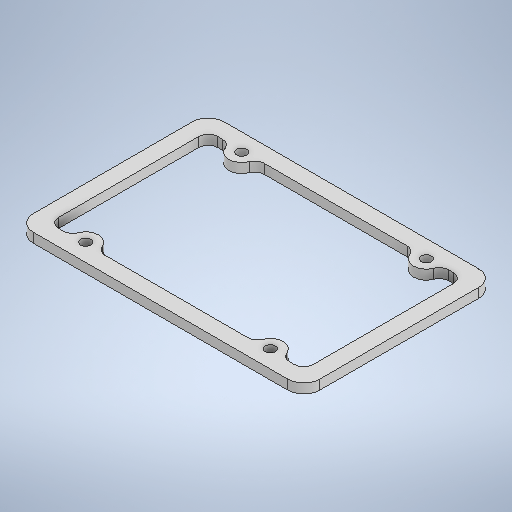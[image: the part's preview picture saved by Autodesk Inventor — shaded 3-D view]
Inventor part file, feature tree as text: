
AUTODESK INVENTOR PART (.ipt)
format: ipt  version: 2025 (Build 290162000, 162)  size: 311,808 bytes
history: native  units: mm
features: extrude x1, sketch x1
ambient origin geometry x8: Origin, YZ Plane, XZ Plane, XY Plane, X Axis, Y Axis, Z Axis, Center Point
bodies: Solid1 (feature_tree)
feature tree (2):
  extrude  "Extrusion1"  Depth=58.0mm
  sketch  "Sketch1"  dims[d0=3.2mm d1=58.0mm d2=49.0mm d3=5.0mm d4=90.0mm d5=60.0mm d6=5.0mm d7=8.0mm d8=5.0mm d9=5.0mm d10=5.0mm d11=3.0mm d12=3.0mm d13=0.0mm]
